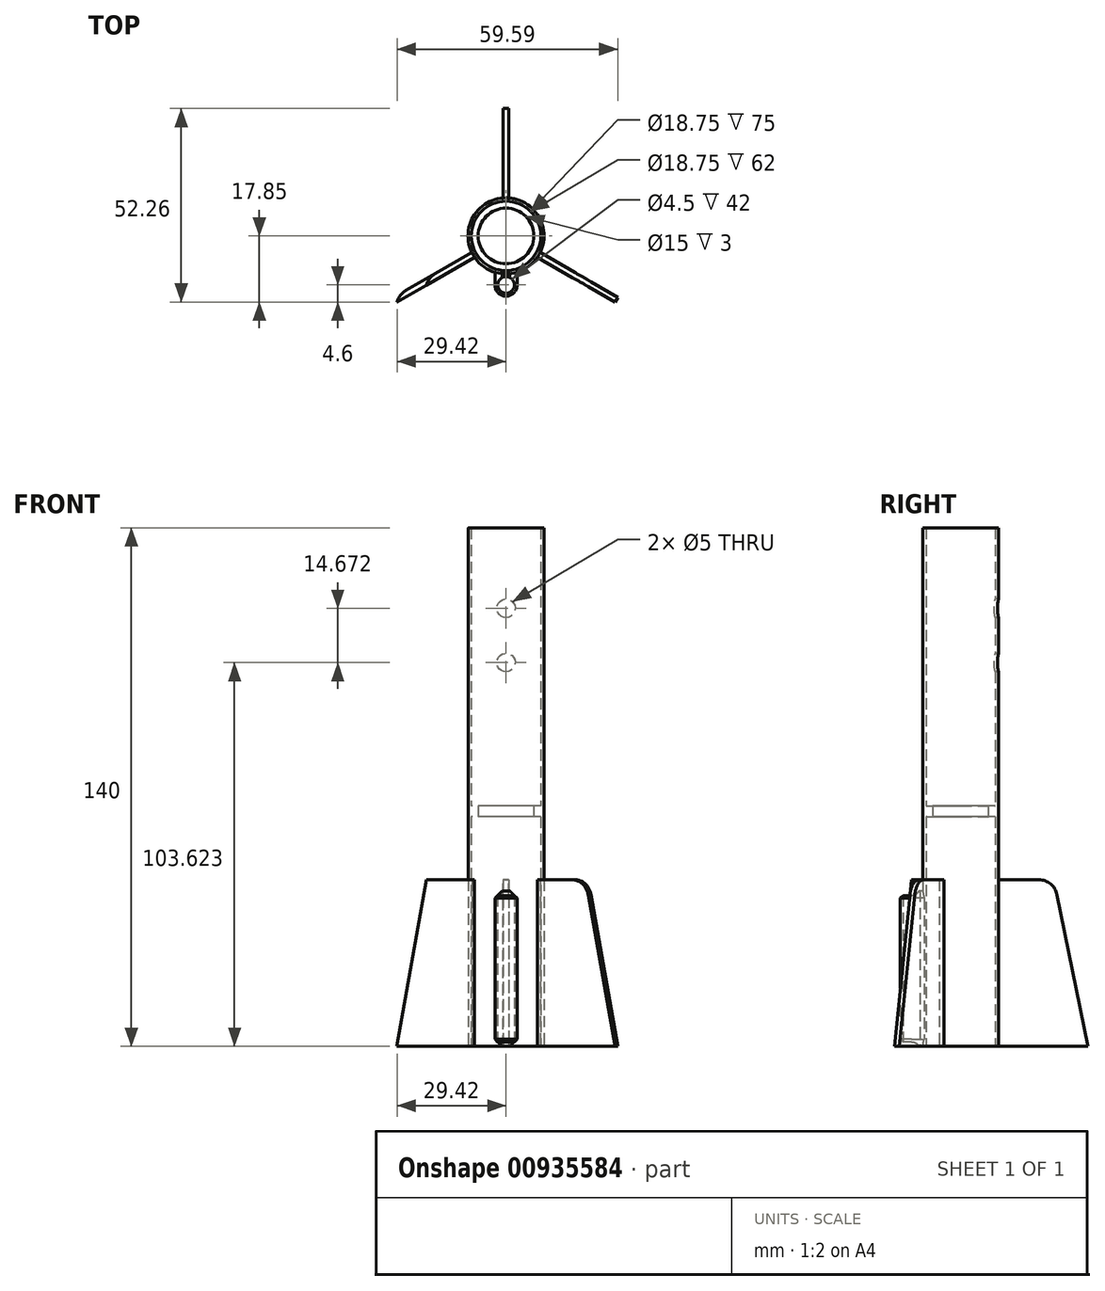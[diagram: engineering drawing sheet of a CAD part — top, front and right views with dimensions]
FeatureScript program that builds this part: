
annotation { "Feature Type Name" : "Feature", "Feature Type Description" : "" }
export const myFeature = defineFeature(function(context is Context, id is Id, definition is map)
    precondition{}
    {
        {
            var Q0;
            Q0=qCreatedBy(makeId("Top.planeOp"),FACE);
            var sketch = newSketch(context, id + "F0", { "sketchPlane" : qUnion([Q0])});
            skCircle(sketch, "E0", {"center": v(0, 0) * mm, "radius": 9.38 * mm});
            skCircle(sketch, "E1", {"center": v(0, 0) * mm, "radius": 10.25 * mm});
            skCircle(sketch, "E2", {"center": v(0, -13.25) * mm, "radius": 2.25 * mm});
            skCircle(sketch, "E3", {"center": v(0, -13.25) * mm, "radius": 3 * mm});
            skLineSegment(sketch, "E4", {"start": v(-3, -13.25) * mm, "end": v(-3, -9.8) * mm});
            skLineSegment(sketch, "E5", {"start": v(3, -13.25) * mm, "end": v(3, -9.8) * mm});
            skLineSegment(sketch, "E6.bottom", {"start": v(-0.75, 35.22) * mm, "end": v(0.75, 35.22) * mm});
            skLineSegment(sketch, "E6.left", {"start": v(-0.75, 35.22) * mm, "end": v(-0.75, 10.22) * mm});
            skLineSegment(sketch, "E6.right", {"start": v(0.75, 35.22) * mm, "end": v(0.75, 10.22) * mm});
            skCircle(sketch, "E7", {"center": v(0, 0) * mm, "radius": 7.5 * mm});
            skSolve(sketch);
        }
        {
            var Q0;
            Q0=makeQuery(id+"F0.imprint","IMPRINT",FACE,{"disambiguationData":[TD([[makeQuery(id+"F0.imprint","IMPRINT",EDGE,{"derivedFrom":sQuery(id+"F0.wireOp",EDGE,"E0")}),-1.0]])]});
            extrude(context, id + "F1", {"entities" : qUnion([Q0]), "depth" : 140 * mm, "offsetDistance" : 25 * mm});
        }
        {
            var Q0;
            Q0=makeQuery(id+"F0.imprint","IMPRINT",FACE,{"disambiguationData":[TD([[makeQuery(id+"F0.imprint","IMPRINT",EDGE,{"derivedFrom":sQuery(id+"F0.wireOp",EDGE,"E6.bottom")}),-1.0]])]});
            extrude(context, id + "F2", {"entities" : qUnion([Q0]), "operationType" : NewBodyOperationType.ADD, "depth" : 45 * mm, "offsetDistance" : 25 * mm});
        }
        {
            var Q0;
            Q0=makeQuery(id+"F2.opExtrude","CAP_EDGE",EDGE,{"disambiguationData":[OSD([sQuery(id+"F0.wireOp",EDGE,"E6.bottom")])],"isStart":false});
            chamfer(context, id + "F3", {"entities" : qUnion([Q0]), "chamferType" : ChamferType.TWO_OFFSETS, "width1" : 49 * mm, "oppositeDirection" : false, "width2" : 10 * mm, "tangentPropagation" : true});
        }
        {
            var Q0;
            Q0=makeQuery(id+"F1.opExtrude","SWEPT_BODY",BODY,{"disambiguationData":[OSD([sQuery(id+"F0.wireOp",EDGE,"E0"),sQuery(id+"F0.wireOp",EDGE,"E1")])]});
            var Q1;
            Q1=makeQuery(id+"F1.opExtrude","CAP_EDGE",EDGE,{"disambiguationData":[OSD([sQuery(id+"F0.wireOp",EDGE,"E0")])],"isStart":false});
            circularPattern(context, id + "F4", {"entities" : qUnion([Q0]), "axis" : qUnion([Q1]), "angle" : 360 * degree, "instanceCount" : 3, "equalSpace" : true});
        }
        {
            var Q0;
            {var subQ0=sQuery(id+"F0.wireOp",EDGE,"E5");Q0=makeQuery(id+"F0.imprint","IMPRINT",FACE,{"disambiguationData":[TD([[makeQuery(id+"F0.imprint","IMPRINT",EDGE,{"derivedFrom":subQ0}),1.0]])]});}
            var Q1;
            {var subQ0=sQuery(id+"F0.wireOp",EDGE,"E4");Q1=makeQuery(id+"F0.imprint","IMPRINT",FACE,{"disambiguationData":[TD([[makeQuery(id+"F0.imprint","IMPRINT",EDGE,{"derivedFrom":subQ0}),-1.0]])]});}
            var Q2;
            Q2=makeQuery(id+"F0.imprint","IMPRINT",FACE,{"disambiguationData":[TD([[makeQuery(id+"F0.imprint","IMPRINT",EDGE,{"derivedFrom":sQuery(id+"F0.wireOp",EDGE,"E2")}),-1.0]])]});
            extrude(context, id + "F5", {"entities" : qUnion([Q0, Q1, Q2]), "operationType" : NewBodyOperationType.ADD, "depth" : 42 * mm, "offsetDistance" : 25 * mm});
        }
        {
            var Q0;
            Q0=makeQuery(id+"F5.opExtrude","CAP_EDGE",EDGE,{"disambiguationData":[OSD([sQuery(id+"F0.wireOp",EDGE,"E3")])],"isStart":false});
            var Q1;
            Q1=makeQuery(id+"F5.opExtrude","CAP_EDGE",EDGE,{"disambiguationData":[OSD([sQuery(id+"F0.wireOp",EDGE,"E3")])],"isStart":true});
            chamfer(context, id + "F6", {"entities" : qUnion([Q0, Q1]), "width" : 2 * mm, "tangentPropagation" : true});
        }
        {
            var Q0;
            Q0=makeQuery(id+"F0.imprint","IMPRINT",FACE,{"disambiguationData":[TD([[makeQuery(id+"F0.imprint","IMPRINT",EDGE,{"derivedFrom":sQuery(id+"F0.wireOp",EDGE,"E0")}),1.0]])]});
            extrude(context, id + "F7", {"entities" : qUnion([Q0]), "operationType" : NewBodyOperationType.ADD, "depth" : 65 * mm, "offsetDistance" : 25 * mm, "hasSecondDirection" : true, "secondDirectionOppositeDirection" : false, "secondDirectionDepth" : 62 * mm});
        }
        {
            var Q0;
            Q0=qCreatedBy(makeId("Front.planeOp"),FACE);
            var sketch = newSketch(context, id + "F8", { "sketchPlane" : qUnion([Q0])});
            skLineSegment(sketch, "E8", {"start": v(0, 118.3) * mm, "end": v(0, 104.39) * mm});
            skSolve(sketch);
        }
        {
            var Q0;
            Q0=sQuery(id+"F8.wireOp",VERTEX,"E8.start");
            var Q1;
            Q1=makeQuery(id+"F1.opExtrude","SWEPT_BODY",BODY,{"disambiguationData":[OSD([sQuery(id+"F0.wireOp",EDGE,"E0"),sQuery(id+"F0.wireOp",EDGE,"E1")])]});
            hole(context, id + "F9", {"style" : HoleStyle.SIMPLE, "endStyle" : HoleEndStyle.THROUGH, "holeDiameter" : 5 * mm, "majorDiameter" : 5 * mm, "isTappedThrough" : true, "tappedDepth" : 12 * mm, "tapClearance" : 3, "locations" : qUnion([Q0]), "scope" : qUnion([Q1])});
        }
        {
            var Q0;
            Q0=qCreatedBy(makeId("Front.planeOp"),FACE);
            var sketch = newSketch(context, id + "F10", { "sketchPlane" : qUnion([Q0])});
            skLineSegment(sketch, "E9", {"start": v(0, 103.62) * mm, "end": v(0, 117.2) * mm});
            skSolve(sketch);
        }
        {
            var Q0;
            Q0=sQuery(id+"F10.wireOp",VERTEX,"E9.start");
            var Q1;
            Q1=makeQuery(id+"F1.opExtrude","SWEPT_BODY",BODY,{"disambiguationData":[OSD([sQuery(id+"F0.wireOp",EDGE,"E0"),sQuery(id+"F0.wireOp",EDGE,"E1")])]});
            hole(context, id + "F11", {"style" : HoleStyle.SIMPLE, "endStyle" : HoleEndStyle.THROUGH, "holeDiameter" : 5 * mm, "majorDiameter" : 5 * mm, "isTappedThrough" : true, "tappedDepth" : 12 * mm, "tapClearance" : 3, "locations" : qUnion([Q0]), "scope" : qUnion([Q1])});
        }
        {
            var Q0;
            {var subQ0=sQuery(id+"F0.wireOp",EDGE,"E6.bottom");Q0=makeQuery(id+"F3.opChamfer","BLEND_EDGE",EDGE,{"blendedFrom":[makeQuery(id+"F2.opExtrude","CAP_EDGE",EDGE,{"disambiguationData":[OSD([subQ0])],"isStart":false}),makeQuery(id+"F2.opExtrude","CAP_FACE",FACE,{"disambiguationData":[OSD([sQuery(id+"F0.wireOp",EDGE,"E1"),subQ0,sQuery(id+"F0.wireOp",EDGE,"E6.left"),sQuery(id+"F0.wireOp",EDGE,"E6.right")])],"isStart":false})],"blendedInto":[makeQuery(id+"F2.opExtrude","CAP_FACE",FACE,{"disambiguationData":[OSD([sQuery(id+"F0.wireOp",EDGE,"E1"),subQ0,sQuery(id+"F0.wireOp",EDGE,"E6.left"),sQuery(id+"F0.wireOp",EDGE,"E6.right")])],"isStart":false})]});}
            var Q1;
            {var subQ0=sQuery(id+"F0.wireOp",EDGE,"E6.bottom");Q1=makeQuery(id+"F4.opPattern","COPY",EDGE,{"derivedFrom":makeQuery(id+"F3.opChamfer","BLEND_EDGE",EDGE,{"blendedFrom":[makeQuery(id+"F2.opExtrude","CAP_EDGE",EDGE,{"disambiguationData":[OSD([subQ0])],"isStart":false}),makeQuery(id+"F2.opExtrude","CAP_FACE",FACE,{"disambiguationData":[OSD([sQuery(id+"F0.wireOp",EDGE,"E1"),subQ0,sQuery(id+"F0.wireOp",EDGE,"E6.left"),sQuery(id+"F0.wireOp",EDGE,"E6.right")])],"isStart":false})],"blendedInto":[makeQuery(id+"F2.opExtrude","CAP_FACE",FACE,{"disambiguationData":[OSD([sQuery(id+"F0.wireOp",EDGE,"E1"),subQ0,sQuery(id+"F0.wireOp",EDGE,"E6.left"),sQuery(id+"F0.wireOp",EDGE,"E6.right")])],"isStart":false})]}),"instanceName":"2"});}
            var Q2;
            Q2=makeQuery(id+"F4.opPattern","COPY",EDGE,{"derivedFrom":makeQuery(id+"F3.opChamfer","BLEND_EDGE",EDGE,{"blendedFrom":[makeQuery(id+"F2.opExtrude","CAP_EDGE",EDGE,{"disambiguationData":[OSD([sQuery(id+"F0.wireOp",EDGE,"E6.bottom")])],"isStart":false}),makeQuery(id+"F2.opExtrude","SWEPT_FACE",FACE,{"disambiguationData":[OSD([sQuery(id+"F0.wireOp",EDGE,"E6.right")])]})],"blendedInto":[makeQuery(id+"F2.opExtrude","SWEPT_FACE",FACE,{"disambiguationData":[OSD([sQuery(id+"F0.wireOp",EDGE,"E6.right")])]})]}),"instanceName":"1"});
            fillet(context, id + "F12", {"entities" : qUnion([Q0, Q1, Q2]), "radius" : 5 * mm, "tangentPropagation" : true, "allowEdgeOverflow" : false});
        }
    });
